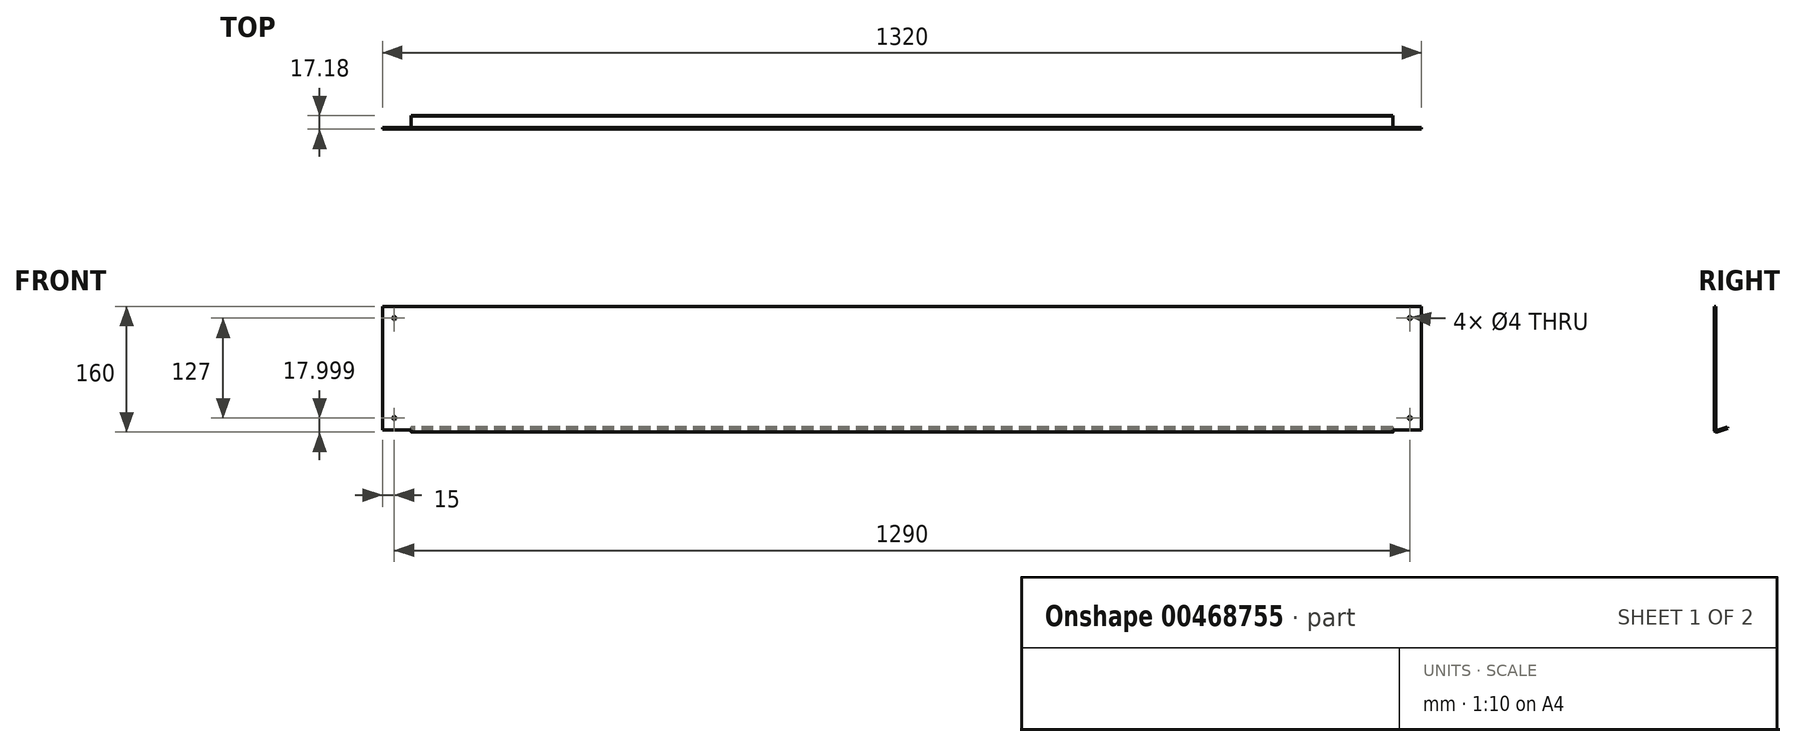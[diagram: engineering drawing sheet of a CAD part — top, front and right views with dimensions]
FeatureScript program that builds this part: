
annotation { "Feature Type Name" : "Feature", "Feature Type Description" : "" }
export const myFeature = defineFeature(function(context is Context, id is Id, definition is map)
    precondition{}
    {
        {
            var Q0;
            Q0=qCreatedBy(makeId("Right.planeOp"),FACE);
            var sketch = newSketch(context, id + "F0", { "sketchPlane" : qUnion([Q0])});
            skLineSegment(sketch, "E0", {"start": v(-2.92, 122.65) * mm, "end": v(-2.92, -34.35) * mm});
            skLineSegment(sketch, "E1", {"start": v(1.1, -37.17) * mm, "end": v(14.26, -32.38) * mm});
            skPoint(sketch, "E2.visualSharp", {"position": v(-2.92, -38.64) * mm});
            skArc(sketch, "E2.filletArc", {"start": v(-2.92, -34.35) * mm, "mid": v(-1.64, -36.8) * mm, "end": v(1.1, -37.17) * mm});
            skLineSegment(sketch, "E3.0", {"start": v(0.42, -35.3) * mm, "end": v(13.57, -30.5) * mm});
            skLineSegment(sketch, "E3.1", {"start": v(-0.92, 122.65) * mm, "end": v(-0.92, -34.35) * mm});
            skPoint(sketch, "E4.visualSharp", {"position": v(-0.92, -35.78) * mm});
            skArc(sketch, "E4.filletArc", {"start": v(-0.92, -34.35) * mm, "mid": v(-0.5, -35.17) * mm, "end": v(0.42, -35.3) * mm});
            skLineSegment(sketch, "E5", {"start": v(13.57, -30.5) * mm, "end": v(14.26, -32.38) * mm});
            skLineSegment(sketch, "E6", {"start": v(-2.92, 122.65) * mm, "end": v(-0.92, 122.65) * mm});
            skSolve(sketch);
        }
        {
            var Q0;
            Q0 = qSketchRegion(id + "F0", true);
            extrude(context, id + "F1", {"entities" : qUnion([Q0]), "depth" : 1247 * mm});
        }
        {
            var Q0;
            Q0=makeQuery(id+"F1.opExtrude","CAP_FACE",FACE,{"disambiguationData":[OSD([sQuery(id+"F0.wireOp",EDGE,"E0"),sQuery(id+"F0.wireOp",EDGE,"E1"),sQuery(id+"F0.wireOp",EDGE,"E2.filletArc"),sQuery(id+"F0.wireOp",EDGE,"E3.0"),sQuery(id+"F0.wireOp",EDGE,"E3.1"),sQuery(id+"F0.wireOp",EDGE,"E4.filletArc"),sQuery(id+"F0.wireOp",EDGE,"E5"),sQuery(id+"F0.wireOp",EDGE,"E6")])],"isStart":false});
            var sketch = newSketch(context, id + "F2", { "sketchPlane" : qUnion([Q0])});
            skLineSegment(sketch, "E7.bottom", {"start": v(-2.92, 122.65) * mm, "end": v(-0.92, 122.65) * mm});
            skLineSegment(sketch, "E7.top", {"start": v(-2.92, -34.35) * mm, "end": v(-0.92, -34.35) * mm});
            skLineSegment(sketch, "E7.left", {"start": v(-2.92, 122.65) * mm, "end": v(-2.92, -34.35) * mm});
            skLineSegment(sketch, "E7.right", {"start": v(-0.92, 122.65) * mm, "end": v(-0.92, -34.35) * mm});
            skSolve(sketch);
        }
        {
            var Q0;
            Q0 = qSketchRegion(id + "F2", true);
            extrude(context, id + "F3", {"entities" : qUnion([Q0]), "operationType" : NewBodyOperationType.ADD, "depth" : 36.5 * mm});
        }
        {
            var Q0;
            Q0=makeQuery(id+"F1.opExtrude","CAP_FACE",FACE,{"disambiguationData":[OSD([sQuery(id+"F0.wireOp",EDGE,"E0"),sQuery(id+"F0.wireOp",EDGE,"E1"),sQuery(id+"F0.wireOp",EDGE,"E2.filletArc"),sQuery(id+"F0.wireOp",EDGE,"E3.0"),sQuery(id+"F0.wireOp",EDGE,"E3.1"),sQuery(id+"F0.wireOp",EDGE,"E4.filletArc"),sQuery(id+"F0.wireOp",EDGE,"E5"),sQuery(id+"F0.wireOp",EDGE,"E6")])],"isStart":true});
            var sketch = newSketch(context, id + "F4", { "sketchPlane" : qUnion([Q0])});
            skLineSegment(sketch, "E8.bottom", {"start": v(2.92, 122.65) * mm, "end": v(0.92, 122.65) * mm});
            skLineSegment(sketch, "E8.top", {"start": v(2.92, -34.35) * mm, "end": v(0.92, -34.35) * mm});
            skLineSegment(sketch, "E8.left", {"start": v(2.92, 122.65) * mm, "end": v(2.92, -34.35) * mm});
            skLineSegment(sketch, "E8.right", {"start": v(0.92, 122.65) * mm, "end": v(0.92, -34.35) * mm});
            skSolve(sketch);
        }
        {
            var Q0;
            Q0 = qSketchRegion(id + "F4", true);
            extrude(context, id + "F5", {"entities" : qUnion([Q0]), "operationType" : NewBodyOperationType.ADD, "depth" : 36.5 * mm});
        }
        {
            var Q0;
            Q0=makeQuery(id+"F5.boolean.opBoolean","MERGE",FACE,{"derivedFrom":[makeQuery(id+"F3.boolean.opBoolean","MERGE",FACE,{"derivedFrom":[makeQuery(id+"F1.opExtrude","SWEPT_FACE",FACE,{"disambiguationData":[OSD([sQuery(id+"F0.wireOp",EDGE,"E0")])]}),makeQuery(id+"F3.opExtrude","SWEPT_FACE",FACE,{"disambiguationData":[OSD([sQuery(id+"F2.wireOp",EDGE,"E7.left")])]})]}),makeQuery(id+"F5.opExtrude","SWEPT_FACE",FACE,{"disambiguationData":[OSD([sQuery(id+"F4.wireOp",EDGE,"E8.left")])]})]});
            var sketch = newSketch(context, id + "F6", { "sketchPlane" : qUnion([Q0])});
            skCircle(sketch, "E9", {"center": v(-21.5, 107.65) * mm, "radius": 2 * mm});
            skCircle(sketch, "E10", {"center": v(-21.5, -19.35) * mm, "radius": 2 * mm});
            skCircle(sketch, "E11", {"center": v(1268.5, 107.65) * mm, "radius": 2 * mm});
            skCircle(sketch, "E12", {"center": v(1268.5, -19.35) * mm, "radius": 2 * mm});
            skSolve(sketch);
        }
        {
            var Q0;
            Q0 = qSketchRegion(id + "F6", true);
            extrude(context, id + "F7", {"entities" : qUnion([Q0]), "operationType" : NewBodyOperationType.REMOVE, "endBound" : BoundingType.THROUGH_ALL, "oppositeDirection" : true, "depth" : 25 * mm});
        }
    });
